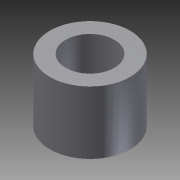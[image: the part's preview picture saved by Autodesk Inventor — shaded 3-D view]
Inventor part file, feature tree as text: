
AUTODESK INVENTOR PART (.ipt)
format: ipt  version: 2014 SP1 (Build 180222100, 222)  size: 97,280 bytes
history: native  units: in
note: dims shown in document units (in); Inventor stores cm internally (conversion verified against a paired STEP export)
features: extrude x2, sketch x2, other x1, imported_body x1
ambient origin geometry x8: Origin, YZ Plane, XZ Plane, XY Plane, X Axis, Y Axis, Z Axis, Center Point
bodies: Body1 (feature_tree)
feature tree (6):
  parser-record x1  (decoder bookkeeping rows leaked as tree rows — omitted from the tree; the rows remain in map.json)
  imported_body  "Base1"
  extrude  "Extrusion1"  Depth=1.0in TaperAngle=0.0deg
  extrude  "Extrusion2"  [1 undecoded]
  sketch  "Sketch1"  dims[d0=0.32in d1=1.0in d2=0.0in]
  sketch  "Sketch2"  dims[d3=0.25in d4=0.0in]
note: 1 required parameter value undecoded (feature->parameter linkage not recoverable at this tier; creation-order binding heuristic only, values carry confidence <= 0.55)
